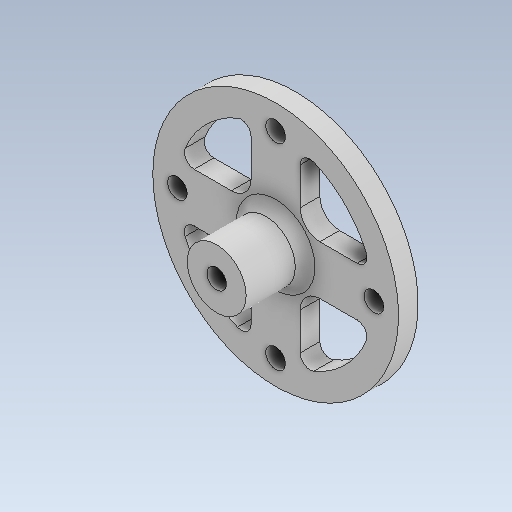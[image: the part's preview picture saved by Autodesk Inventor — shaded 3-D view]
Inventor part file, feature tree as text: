
AUTODESK INVENTOR PART (.ipt)
format: ipt  version: 2020 (Build 240168000, 168)  size: 249,856 bytes
history: native  units: mm
features: sketch x5, extrude x4, other x4, fillet x3, projected_geometry x2, hole x1, pattern_circular x1, reference x1
ambient origin geometry x8: Origin, YZ Plane, XZ Plane, XY Plane, X Axis, Y Axis, Z Axis, Center Point
bodies: Solid1 (feature_tree)
feature tree (21):
  extrude  "Extrusion1"  Depth=5.0mm
  hole  "Hole1"  [1 undecoded]
  extrude  "Extrusion2"  Depth=2.0mm
  fillet  "Fillet1"  Radius=1.0mm
  fillet  "Fillet2"  Radius=2.0mm
  extrude  "Extrusion3"  Depth=1.0mm
  extrude  "Extrusion4"  Depth=1.0mm
  pattern_circular  "Circular Pattern1"  [2 undecoded]
  fillet  "Fillet3"  Radius=40.0mm
  sketch  "Sketch1"  dims[d0=5.0mm d1=5.0mm]
  reference  "Reference1"
  sketch  "Sketch2"  dims[d2=2.0mm d3=0.0mm]
  projected_geometry  "Projected Loop1"
  sketch  "Sketch3"  dims[d4=2.0mm d5=6.0mm d6=4.0mm d7=2.0mm d8=90.0deg d9=5.0mm d10=0.0mm d11=6.0mm]
  sketch  "Sketch4"  dims[d12=6.0mm d13=0.0mm d14=2.0mm d15=1.0mm d16=2.0mm]
  sketch  "Sketch5"  dims[d17=12.0mm d18=0.0mm d19=25.0mm d20=20.0mm d21=2.0mm d22=0.0mm d23=40.0mm d24=360.0deg d26=1.0mm]
  projected_geometry  "Projected Loop2"
  parser-record x1  (decoder bookkeeping rows leaked as tree rows — omitted from the tree; the rows remain in map.json)
  other  "reducer_1.iam"
  other  "mot_27_ass:1"
  other  "mot_27_1:1"
note: 3 required parameter values undecoded (feature->parameter linkage not recoverable at this tier; creation-order binding heuristic only, values carry confidence <= 0.55)
note: 1 file-system path scrubbed to <path> (originals preserved in map.json)
